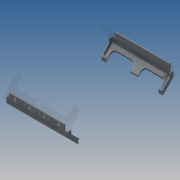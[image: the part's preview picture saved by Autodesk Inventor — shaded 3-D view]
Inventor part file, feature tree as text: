
AUTODESK INVENTOR PART (.ipt)
format: ipt  version: 2016 SP2 (Build 200236200, 236)  size: 1,109,504 bytes
history: native  units: in
note: dims shown in document units (in); Inventor stores cm internally (conversion verified against a paired STEP export)
features: extrude x11, sketch x7, plane x3, mirror x1, fillet x1
ambient origin geometry x8: Origin, YZ Plane, XZ Plane, XY Plane, X Axis, Y Axis, Z Axis, Center Point
bodies: Solid1 (feature_tree)
feature tree (23):
  sketch  "Sketch2"  dims[d0=4.063in d1=0.1559in]
  extrude  "Extrusion1"  Depth=0.1559in
  extrude  "Extrusion2"  Depth=0.0472in
  extrude  "Extrusion3"  Depth=0.0157in
  extrude  "Extrusion4"  Depth=0.6457in
  plane  "Work Plane1"
  extrude  "Extrusion5"  TaperAngle=135.0deg  [1 undecoded]
  mirror  "Mirror1"
  extrude  "Extrusion6"  TaperAngle=0.0deg  [1 undecoded]
  plane  "Work Plane2"
  sketch  "Sketch5"  dims[d6=0.4567in d7=0.6457in]
  extrude  "Extrusion7"  Depth=0.0in TaperAngle=0.0deg
  extrude  "Extrusion8"  Depth=0.0in TaperAngle=0.0deg
  plane  "Work Plane3"
  extrude  "Extrusion9"  Depth=0.0in TaperAngle=0.0deg
  fillet  "Fillet1"  [1 undecoded]
  extrude  "Extrusion10"  Depth=0.0in
  extrude  "Extrusion11"  Depth=0.0in
  sketch  "Sketch3"  dims[d2=0.1575in d3=0.0472in]
  sketch  "Sketch4"  dims[d4=0.2205in d5=0.0157in]
  sketch  "Sketch7"  dims[d8=0.3307in d9=135.0deg]
  sketch  "Sketch8"  dims[d10=2.5197in d11=0.0in]
  sketch  "Sketch9"  dims[d12=0.0445in d13=2.4252in d14=0.0in d15=2.1732in d16=0.0in d17=2.2677in d18=0.0in d19=0.0in d20=0.2992in d21=0.3465in d22=0.1417in d23=0.0787in d24=2.2677in d25=0.0in d27=2.2677in d28=0.0in d29=0.1969in d30=2.2677in d31=0.0in d32=2.2677in d33=0.0in d34=0.2677in d37=0.1417in d38=2.2677in d39=0.0in d40=0.0039in d41=0.3465in d42=0.3937in d43=0.0315in d44=0.0315in d45=0.0079in d46=0.0079in d47=0.1732in d48=0.0394in d49=1.5748in d51=0.5984in d52=0.3937in d54=0.3937in d56=0.3937in d57=0.0315in d58=0.0079in d59=0.0079in d60=0.1732in d61=0.0394in d62=0.0in d63=0.0in d64=0.0315in d65=1.5748in d67=0.4409in d68=0.3937in d70=0.3937in d72=0.0339in d73=0.0551in d74=0.3071in d75=0.0in d76=0.0in]
note: 3 required parameter values undecoded (feature->parameter linkage not recoverable at this tier; creation-order binding heuristic only, values carry confidence <= 0.55)
